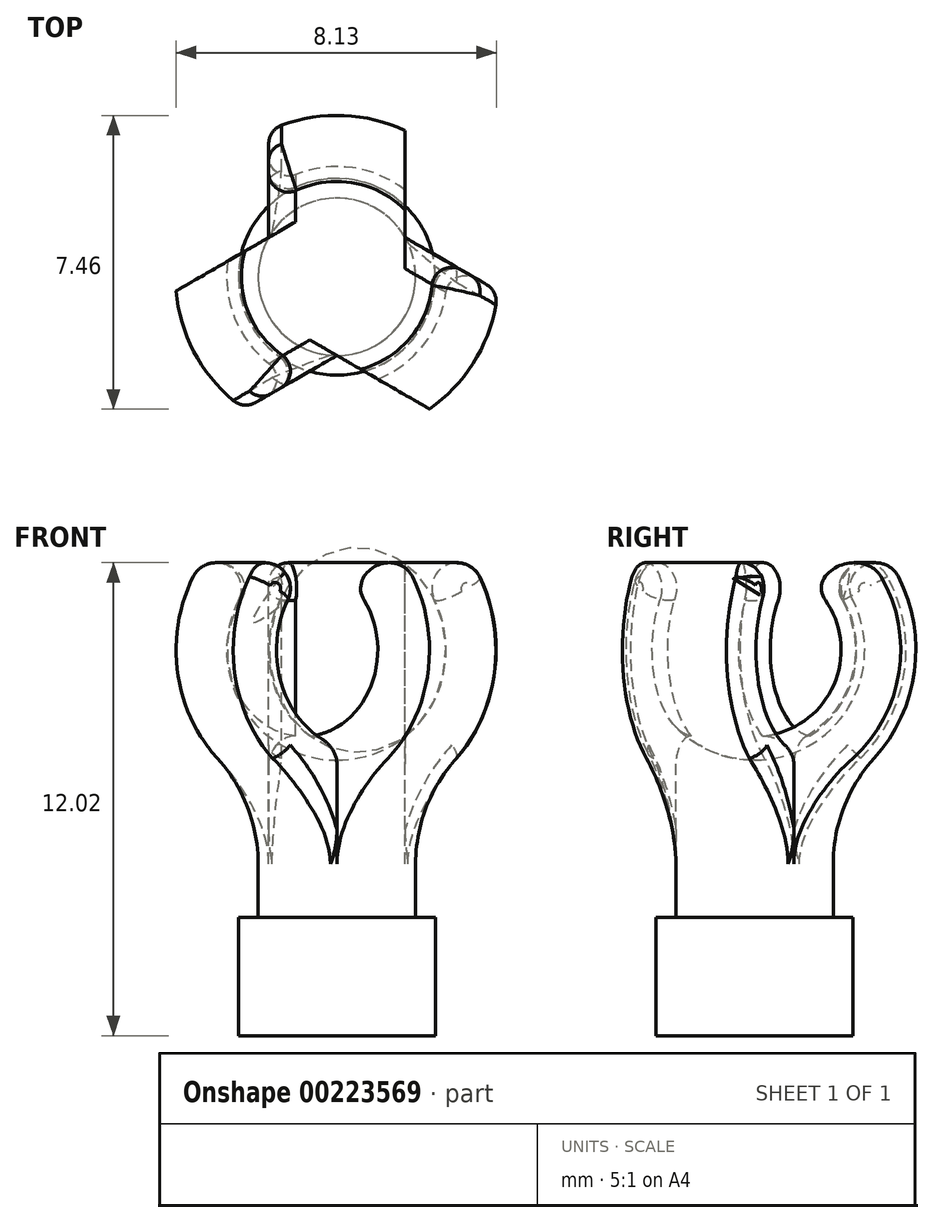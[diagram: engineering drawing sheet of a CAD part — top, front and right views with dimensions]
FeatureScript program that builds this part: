
annotation { "Feature Type Name" : "Feature", "Feature Type Description" : "" }
export const myFeature = defineFeature(function(context is Context, id is Id, definition is map)
    precondition{}
    {
        {
            var Q0;
            Q0=qCreatedBy(makeId("Right.planeOp"),FACE);
            var sketch = newSketch(context, id + "F0", { "sketchPlane" : qUnion([Q0])});
            skArc(sketch, "E0", {"start": v(-3.65, 1.86) * mm, "mid": v(-3.5, -2.14) * mm, "end": v(0, -4.1) * mm});
            skArc(sketch, "E1", {"start": v(-2.5, 1.27) * mm, "mid": v(-2.39, -1.46) * mm, "end": v(0, -2.8) * mm});
            skLineSegment(sketch, "E2", {"start": v(0, -2.8) * mm, "end": v(0, -4.1) * mm});
            skLineSegment(sketch, "E3", {"start": v(0, 0) * mm, "end": v(-3.65, 1.86) * mm, "construction": true});
            skPoint(sketch, "E4.end.orphan", {"position": v(0, 2.8) * mm});
            skPoint(sketch, "E4.start.orphan", {"position": v(0, 4.1) * mm});
            skArc(sketch, "E5", {"start": v(-2.5, 1.27) * mm, "mid": v(-2.78, 2.15) * mm, "end": v(-3.65, 1.86) * mm});
            skCircle(sketch, "E6", {"center": v(0, 0) * mm, "radius": 2.5 * mm, "construction": true});
            skLineSegment(sketch, "E7", {"start": v(-2.5, 0) * mm, "end": v(-2.5, 2.5) * mm, "construction": true});
            skLineSegment(sketch, "E8", {"start": v(0, 2.5) * mm, "end": v(-2.5, 2.5) * mm, "construction": true});
            skSolve(sketch);
        }
        {
            var Q0;
            Q0=makeQuery(id+"F0.imprint","IMPRINT",FACE,{"disambiguationData":[TD([[makeQuery(id+"F0.imprint","IMPRINT",EDGE,{"derivedFrom":sQuery(id+"F0.wireOp",EDGE,"E0")}),1.0]])]});
            var Q1;
            Q1=sQuery(id+"F0.wireOp",EDGE,"E2");
            revolve(context, id + "F1", {"entities" : qUnion([Q0]), "axis" : qUnion([Q1]), "revolveType" : RevolveType.FULL});
        }
        {
            var Q0;
            Q0=qCreatedBy(makeId("Top.planeOp"),FACE);
            var sketch = newSketch(context, id + "F2", { "sketchPlane" : qUnion([Q0])});
            skLineSegment(sketch, "E9", {"start": v(0, 0) * mm, "end": v(19.8, 11.43) * mm, "construction": true});
            skLineSegment(sketch, "E10", {"start": v(1.73, 1) * mm, "end": v(1.73, 9.08) * mm});
            skLineSegment(sketch, "E11", {"start": v(1.73, 9.08) * mm, "end": v(5.23, 3.02) * mm});
            skLineSegment(sketch, "E12.MirrorCS", {"start": v(1.73, 1) * mm, "end": v(8.73, -3.04) * mm});
            skLineSegment(sketch, "E13.MirrorCS", {"start": v(8.73, -3.04) * mm, "end": v(5.23, 3.02) * mm});
            skLineSegment(sketch, "E14.1.0", {"start": v(-1.73, 1) * mm, "end": v(-1.73, 9.08) * mm});
            skLineSegment(sketch, "E14.1.1", {"start": v(-1.73, 1) * mm, "end": v(-8.73, -3.04) * mm});
            skLineSegment(sketch, "E14.1.2", {"start": v(-8.73, -3.04) * mm, "end": v(-5.23, 3.02) * mm});
            skLineSegment(sketch, "E14.1.3", {"start": v(-1.73, 9.08) * mm, "end": v(-5.23, 3.02) * mm});
            skLineSegment(sketch, "E14.2.0", {"start": v(0, -2) * mm, "end": v(-7, -6.04) * mm});
            skLineSegment(sketch, "E14.2.1", {"start": v(0, -2) * mm, "end": v(7, -6.04) * mm});
            skLineSegment(sketch, "E14.2.2", {"start": v(7, -6.04) * mm, "end": v(0, -6.04) * mm});
            skLineSegment(sketch, "E14.2.3", {"start": v(-7, -6.04) * mm, "end": v(0, -6.04) * mm});
            skPoint(sketch, "E14.center", {"position": v(0, 0) * mm});
            skSolve(sketch);
        }
        {
            var Q0;
            Q0 = qSketchRegion(id + "F2", true);
            extrude(context, id + "F3", {"entities" : qUnion([Q0]), "operationType" : NewBodyOperationType.REMOVE, "oppositeDirection" : true, "depth" : 25 * mm, "hasSecondDirection" : true, "secondDirectionOppositeDirection" : false, "secondDirectionDepth" : 25 * mm});
        }
        {
            var Q0;
            Q0=qCreatedBy(makeId("Front.planeOp"),FACE);
            var sketch = newSketch(context, id + "F4", { "sketchPlane" : qUnion([Q0])});
            skLineSegment(sketch, "E15.bottom", {"start": v(0, -2.8) * mm, "end": v(2, -2.8) * mm});
            skLineSegment(sketch, "E15.top", {"start": v(0, -6.8) * mm, "end": v(2, -6.8) * mm});
            skLineSegment(sketch, "E15.left", {"start": v(0, -2.8) * mm, "end": v(0, -6.8) * mm});
            skLineSegment(sketch, "E15.right", {"start": v(2, -2.8) * mm, "end": v(2, -6.8) * mm});
            skSolve(sketch);
        }
        {
            var Q0;
            Q0 = qSketchRegion(id + "F4", true);
            var Q1;
            Q1=sQuery(id+"F4.wireOp",EDGE,"E15.left");
            revolve(context, id + "F5", {"operationType" : NewBodyOperationType.ADD, "entities" : qUnion([Q0]), "axis" : qUnion([Q1]), "revolveType" : RevolveType.FULL});
        }
        {
            var Q0;
            Q0=makeQuery(id+"F5.boolean.opBoolean","INTERSECT",EDGE,{"disambiguationData":[OD(2.0)],"derivedFrom":[makeQuery(id+"F1.opRevolve","SWEPT_FACE",FACE,{"disambiguationData":[OSD([sQuery(id+"F0.wireOp",EDGE,"E0")])]}),makeQuery(id+"F5.opRevolve","SWEPT_FACE",FACE,{"disambiguationData":[OSD([sQuery(id+"F4.wireOp",EDGE,"E15.right")])]})]});
            var Q1;
            Q1=makeQuery(id+"F5.boolean.opBoolean","INTERSECT",EDGE,{"disambiguationData":[OD(1.0)],"derivedFrom":[makeQuery(id+"F1.opRevolve","SWEPT_FACE",FACE,{"disambiguationData":[OSD([sQuery(id+"F0.wireOp",EDGE,"E0")])]}),makeQuery(id+"F5.opRevolve","SWEPT_FACE",FACE,{"disambiguationData":[OSD([sQuery(id+"F4.wireOp",EDGE,"E15.right")])]})]});
            var Q2;
            Q2=makeQuery(id+"F5.boolean.opBoolean","INTERSECT",EDGE,{"disambiguationData":[OD(0.0)],"derivedFrom":[makeQuery(id+"F1.opRevolve","SWEPT_FACE",FACE,{"disambiguationData":[OSD([sQuery(id+"F0.wireOp",EDGE,"E0")])]}),makeQuery(id+"F5.opRevolve","SWEPT_FACE",FACE,{"disambiguationData":[OSD([sQuery(id+"F4.wireOp",EDGE,"E15.right")])]})]});
            fillet(context, id + "F6", {"entities" : qUnion([Q0, Q1, Q2]), "radius" : 4 * mm, "tangentPropagation" : true, "allowEdgeOverflow" : false});
        }
        {
            var Q0;
            Q0=makeQuery(id+"F5.opRevolve","SWEPT_FACE",FACE,{"disambiguationData":[OSD([sQuery(id+"F4.wireOp",EDGE,"E15.top")])]});
            var sketch = newSketch(context, id + "F7", { "sketchPlane" : qUnion([Q0])});
            skCircle(sketch, "E16", {"center": v(0, 0) * mm, "radius": 2.5 * mm});
            skSolve(sketch);
        }
        {
            var Q0;
            Q0 = qSketchRegion(id + "F7", true);
            extrude(context, id + "F8", {"entities" : qUnion([Q0]), "operationType" : NewBodyOperationType.ADD, "depth" : 3 * mm});
        }
        {
            var Q0;
            Q0=qCreatedBy(makeId("Top.planeOp"),FACE);
            var sketch = newSketch(context, id + "F9", { "sketchPlane" : qUnion([Q0])});
            skCircle(sketch, "E17.cCircle", {"center": v(0, 0) * mm, "radius": 2.15 * mm, "construction": true});
            skLineSegment(sketch, "E17.0", {"start": v(-1.56, 2.15) * mm, "end": v(1.56, 2.15) * mm});
            skLineSegment(sketch, "E17.1", {"start": v(1.56, 2.15) * mm, "end": v(2.53, -0.82) * mm});
            skLineSegment(sketch, "E17.2", {"start": v(2.53, -0.82) * mm, "end": v(0, -2.66) * mm});
            skLineSegment(sketch, "E17.3", {"start": v(0, -2.66) * mm, "end": v(-2.53, -0.82) * mm});
            skLineSegment(sketch, "E17.4", {"start": v(-2.53, -0.82) * mm, "end": v(-1.56, 2.15) * mm});
            skPoint(sketch, "E17.0.midPoint", {"position": v(0, 2.15) * mm});
            skSolve(sketch);
        }
        {
            var Q0;
            Q0=makeQuery(id+"F3.boolean.opBoolean","INTERSECT",EDGE,{"derivedFrom":[makeQuery(id+"F1.opRevolve","SWEPT_FACE",FACE,{"disambiguationData":[OSD([sQuery(id+"F0.wireOp",EDGE,"E5")])]}),makeQuery(id+"F3.opExtrude","SWEPT_FACE",FACE,{"disambiguationData":[OSD([sQuery(id+"F2.wireOp",EDGE,"E14.2.0")])]})]});
            var Q1;
            Q1=makeQuery(id+"F3.boolean.opBoolean","INTERSECT",EDGE,{"derivedFrom":[makeQuery(id+"F1.opRevolve","SWEPT_FACE",FACE,{"disambiguationData":[OSD([sQuery(id+"F0.wireOp",EDGE,"E5")])]}),makeQuery(id+"F3.opExtrude","SWEPT_FACE",FACE,{"disambiguationData":[OSD([sQuery(id+"F2.wireOp",EDGE,"E14.1.0")])]})]});
            var Q2;
            Q2=makeQuery(id+"F3.boolean.opBoolean","INTERSECT",EDGE,{"derivedFrom":[makeQuery(id+"F1.opRevolve","SWEPT_FACE",FACE,{"disambiguationData":[OSD([sQuery(id+"F0.wireOp",EDGE,"E5")])]}),makeQuery(id+"F3.opExtrude","SWEPT_FACE",FACE,{"disambiguationData":[OSD([sQuery(id+"F2.wireOp",EDGE,"E12.MirrorCS")])]})]});
            fillet(context, id + "F10", {"entities" : qUnion([Q0, Q1, Q2]), "radius" : 0.5 * mm, "tangentPropagation" : true, "allowEdgeOverflow" : false});
        }
    });
